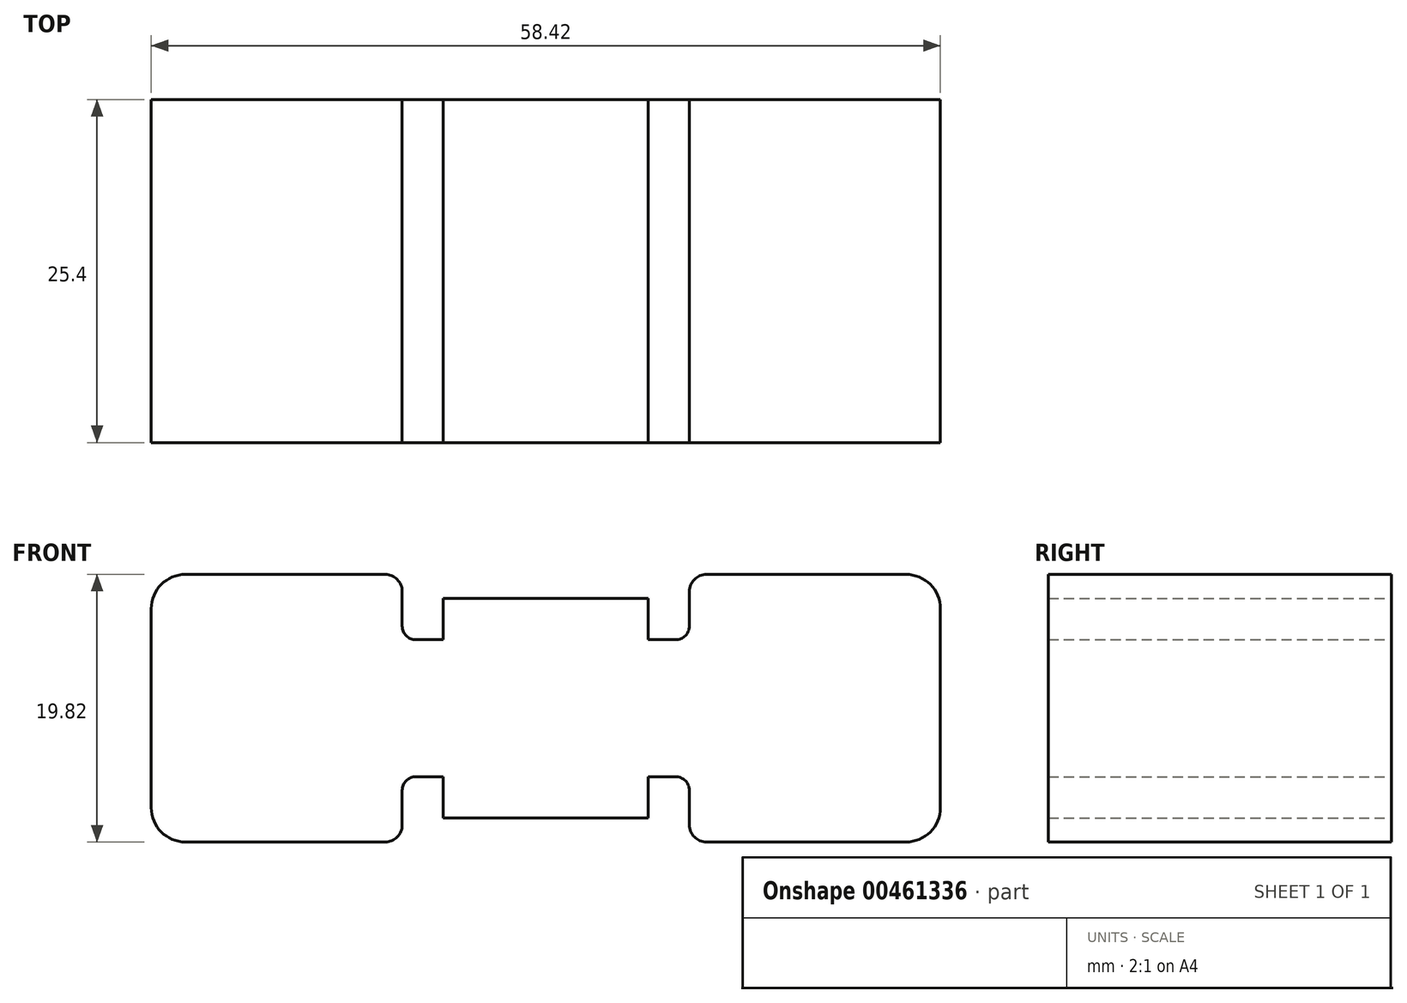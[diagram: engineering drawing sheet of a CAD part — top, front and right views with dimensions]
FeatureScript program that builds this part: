
annotation { "Feature Type Name" : "Feature", "Feature Type Description" : "" }
export const myFeature = defineFeature(function(context is Context, id is Id, definition is map)
    precondition{}
    {
        {
            var Q0;
            Q0=qCreatedBy(makeId("Front.planeOp"),FACE);
            var sketch = newSketch(context, id + "F0", { "sketchPlane" : qUnion([Q0])});
            skLineSegment(sketch, "E0", {"start": v(-29.21, 0) * mm, "end": v(-29.21, 7.37) * mm});
            skLineSegment(sketch, "E1", {"start": v(-26.67, 9.9) * mm, "end": v(-11.9, 9.9) * mm});
            skLineSegment(sketch, "E2", {"start": v(-10.63, 8.64) * mm, "end": v(-10.63, 6.08) * mm});
            skLineSegment(sketch, "E3", {"start": v(-9.61, 5.07) * mm, "end": v(-7.6, 5.07) * mm});
            skLineSegment(sketch, "E4", {"start": v(-7.6, 5.07) * mm, "end": v(-7.6, 8.13) * mm});
            skLineSegment(sketch, "E5", {"start": v(-7.6, 8.13) * mm, "end": v(0, 8.13) * mm});
            skLineSegment(sketch, "E6", {"start": v(0, 8.13) * mm, "end": v(0, 0) * mm});
            skLineSegment(sketch, "E7", {"start": v(0, 0) * mm, "end": v(-29.2, 0) * mm});
            skPoint(sketch, "E8.visualSharp", {"position": v(-29.21, 9.9) * mm});
            skArc(sketch, "E8.filletArc", {"start": v(-26.67, 9.9) * mm, "mid": v(-28.47, 9.16) * mm, "end": v(-29.21, 7.37) * mm});
            skPoint(sketch, "E9.visualSharp", {"position": v(-10.63, 9.9) * mm});
            skArc(sketch, "E9.filletArc", {"start": v(-10.63, 8.64) * mm, "mid": v(-11, 9.53) * mm, "end": v(-11.9, 9.9) * mm});
            skPoint(sketch, "E10.visualSharp", {"position": v(-10.63, 5.07) * mm});
            skArc(sketch, "E10.filletArc", {"start": v(-10.63, 6.08) * mm, "mid": v(-10.33, 5.37) * mm, "end": v(-9.61, 5.07) * mm});
            skLineSegment(sketch, "E11.MirrorCS", {"start": v(7.6, 8.13) * mm, "end": v(0, 8.13) * mm});
            skLineSegment(sketch, "E12.MirrorCS", {"start": v(9.61, 5.07) * mm, "end": v(7.6, 5.07) * mm});
            skPoint(sketch, "E13.MirrorP", {"position": v(10.63, 5.07) * mm});
            skLineSegment(sketch, "E14.MirrorCS", {"start": v(10.63, 8.64) * mm, "end": v(10.63, 6.08) * mm});
            skPoint(sketch, "E15.MirrorP", {"position": v(10.63, 9.9) * mm});
            skArc(sketch, "E16.MirrorCS", {"start": v(10.63, 8.64) * mm, "mid": v(11, 9.53) * mm, "end": v(11.9, 9.9) * mm});
            skLineSegment(sketch, "E17.MirrorCS", {"start": v(26.67, 9.9) * mm, "end": v(11.9, 9.9) * mm});
            skLineSegment(sketch, "E18.MirrorCS", {"start": v(0, 0) * mm, "end": v(29.2, 0) * mm});
            skLineSegment(sketch, "E19.MirrorCS", {"start": v(7.6, 5.07) * mm, "end": v(7.6, 8.13) * mm});
            skArc(sketch, "E20.MirrorCS", {"start": v(10.63, 6.08) * mm, "mid": v(10.33, 5.37) * mm, "end": v(9.61, 5.07) * mm});
            skLineSegment(sketch, "E21.MirrorCS", {"start": v(29.21, 0) * mm, "end": v(29.21, 7.37) * mm});
            skArc(sketch, "E22.MirrorCS", {"start": v(26.67, 9.9) * mm, "mid": v(28.47, 9.16) * mm, "end": v(29.21, 7.37) * mm});
            skLineSegment(sketch, "E23.MirrorCS", {"start": v(7.6, -8.13) * mm, "end": v(0, -8.13) * mm});
            skLineSegment(sketch, "E24.MirrorCS", {"start": v(7.6, -5.07) * mm, "end": v(7.6, -8.13) * mm});
            skLineSegment(sketch, "E25.MirrorCS", {"start": v(9.61, -5.07) * mm, "end": v(7.6, -5.07) * mm});
            skPoint(sketch, "E26.MirrorP", {"position": v(10.63, -5.07) * mm});
            skArc(sketch, "E27.MirrorCS", {"start": v(10.63, -6.08) * mm, "mid": v(10.33, -5.37) * mm, "end": v(9.61, -5.07) * mm});
            skLineSegment(sketch, "E28.MirrorCS", {"start": v(10.63, -8.64) * mm, "end": v(10.63, -6.08) * mm});
            skArc(sketch, "E29.MirrorCS", {"start": v(10.63, -8.64) * mm, "mid": v(11, -9.53) * mm, "end": v(11.9, -9.9) * mm});
            skLineSegment(sketch, "E30.MirrorCS", {"start": v(26.67, -9.9) * mm, "end": v(11.9, -9.9) * mm});
            skArc(sketch, "E31.MirrorCS", {"start": v(26.67, -9.9) * mm, "mid": v(28.47, -9.16) * mm, "end": v(29.21, -7.37) * mm});
            skLineSegment(sketch, "E32.MirrorCS", {"start": v(29.21, 0) * mm, "end": v(29.21, -7.37) * mm});
            skLineSegment(sketch, "E33.MirrorCS", {"start": v(-26.67, -9.9) * mm, "end": v(-11.9, -9.9) * mm});
            skLineSegment(sketch, "E34.MirrorCS", {"start": v(-7.6, -8.13) * mm, "end": v(0, -8.13) * mm});
            skLineSegment(sketch, "E35.MirrorCS", {"start": v(-7.6, -5.07) * mm, "end": v(-7.6, -8.13) * mm});
            skLineSegment(sketch, "E36.MirrorCS", {"start": v(-9.61, -5.07) * mm, "end": v(-7.6, -5.07) * mm});
            skArc(sketch, "E37.MirrorCS", {"start": v(-10.63, -6.08) * mm, "mid": v(-10.33, -5.37) * mm, "end": v(-9.61, -5.07) * mm});
            skLineSegment(sketch, "E38.MirrorCS", {"start": v(-10.63, -8.64) * mm, "end": v(-10.63, -6.08) * mm});
            skArc(sketch, "E39.MirrorCS", {"start": v(-10.63, -8.64) * mm, "mid": v(-11, -9.53) * mm, "end": v(-11.9, -9.9) * mm});
            skArc(sketch, "E40.MirrorCS", {"start": v(-26.67, -9.9) * mm, "mid": v(-28.47, -9.16) * mm, "end": v(-29.21, -7.37) * mm});
            skLineSegment(sketch, "E41.MirrorCS", {"start": v(-29.21, 0) * mm, "end": v(-29.21, -7.37) * mm});
            skSolve(sketch);
        }
        {
            var Q0;
            Q0=makeQuery(id+"F0.imprint","IMPRINT",FACE,{"disambiguationData":[TD([[makeQuery(id+"F0.imprint","IMPRINT",EDGE,{"derivedFrom":sQuery(id+"F0.wireOp",EDGE,"E0")}),-1.0]])]});
            var Q1;
            Q1=makeQuery(id+"F0.imprint","IMPRINT",FACE,{"disambiguationData":[TD([[makeQuery(id+"F0.imprint","IMPRINT",EDGE,{"derivedFrom":sQuery(id+"F0.wireOp",EDGE,"E7")}),1.0]])]});
            var Q2;
            Q2=makeQuery(id+"F0.imprint","IMPRINT",FACE,{"disambiguationData":[TD([[makeQuery(id+"F0.imprint","IMPRINT",EDGE,{"derivedFrom":sQuery(id+"F0.wireOp",EDGE,"E6")}),1.0]])]});
            extrude(context, id + "F1", {"entities" : qUnion([Q0, Q1, Q2]), "depth" : 25.4 * mm});
        }
    });
